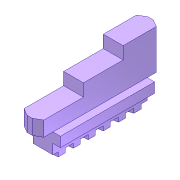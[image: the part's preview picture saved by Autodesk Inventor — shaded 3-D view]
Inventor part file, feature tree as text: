
AUTODESK INVENTOR PART (.ipt)
format: ipt  version: 2016 (Build 200138000, 138)  size: 250,368 bytes
history: native  units: in
note: dims shown in document units (in); Inventor stores cm internally (conversion verified against a paired STEP export)
features: extrude x7, sketch x7, fillet x1, projected_geometry x1
ambient origin geometry x8: Origin, YZ Plane, XZ Plane, XY Plane, X Axis, Y Axis, Z Axis, Center Point
bodies: Solid1 (feature_tree)
feature tree (16):
  extrude  "Extrusion8"  Depth=0.1378in
  extrude  "Extrusion9"  Depth=0.0787in
  extrude  "Extrusion10"  Depth=0.315in
  extrude  "Extrusion11"  TaperAngle=30.0deg  [1 undecoded]
  extrude  "Extrusion13"  Depth=0.7874in TaperAngle=0.0deg
  extrude  "Extrusion14"  Depth=0.1969in TaperAngle=0.0deg
  fillet  "Fillet1"  Radius=0.315in
  extrude  "Extrusion16"  Depth=0.1181in
  sketch  "Sketch10"  dims[d51=0.0787in d52=0.1378in]
  sketch  "Sketch11"  dims[d53=0.0787in d54=0.0787in]
  sketch  "Sketch12"  dims[d55=0.0787in d56=0.315in]
  sketch  "Sketch13"  dims[d57=0.9843in d58=0.0in d59=30.0deg]
  sketch  "Sketch15"  dims[d60=30.0deg d61=0.7874in d62=0.0in]
  sketch  "Sketch16"  dims[d63=0.315in d64=0.1969in d65=0.0in d66=0.315in]
  sketch  "Sketch18"  dims[d67=0.0984in d68=0.0in d72=0.1181in d73=0.1181in d74=0.0787in d75=0.0in d76=0.3661in d79=0.0551in d81=0.0551in d83=0.0551in d85=0.0551in d87=0.0551in d89=0.0551in d90=0.0354in d91=0.0in d92=0.1181in d93=0.1181in d94=0.1181in d95=0.1181in d96=0.1181in d102=0.0008in d103=0.0118in d104=0.0118in d105=0.3937in d106=0.0in]
  projected_geometry  "Projected Loop1"
note: 1 required parameter value undecoded (feature->parameter linkage not recoverable at this tier; creation-order binding heuristic only, values carry confidence <= 0.55)
